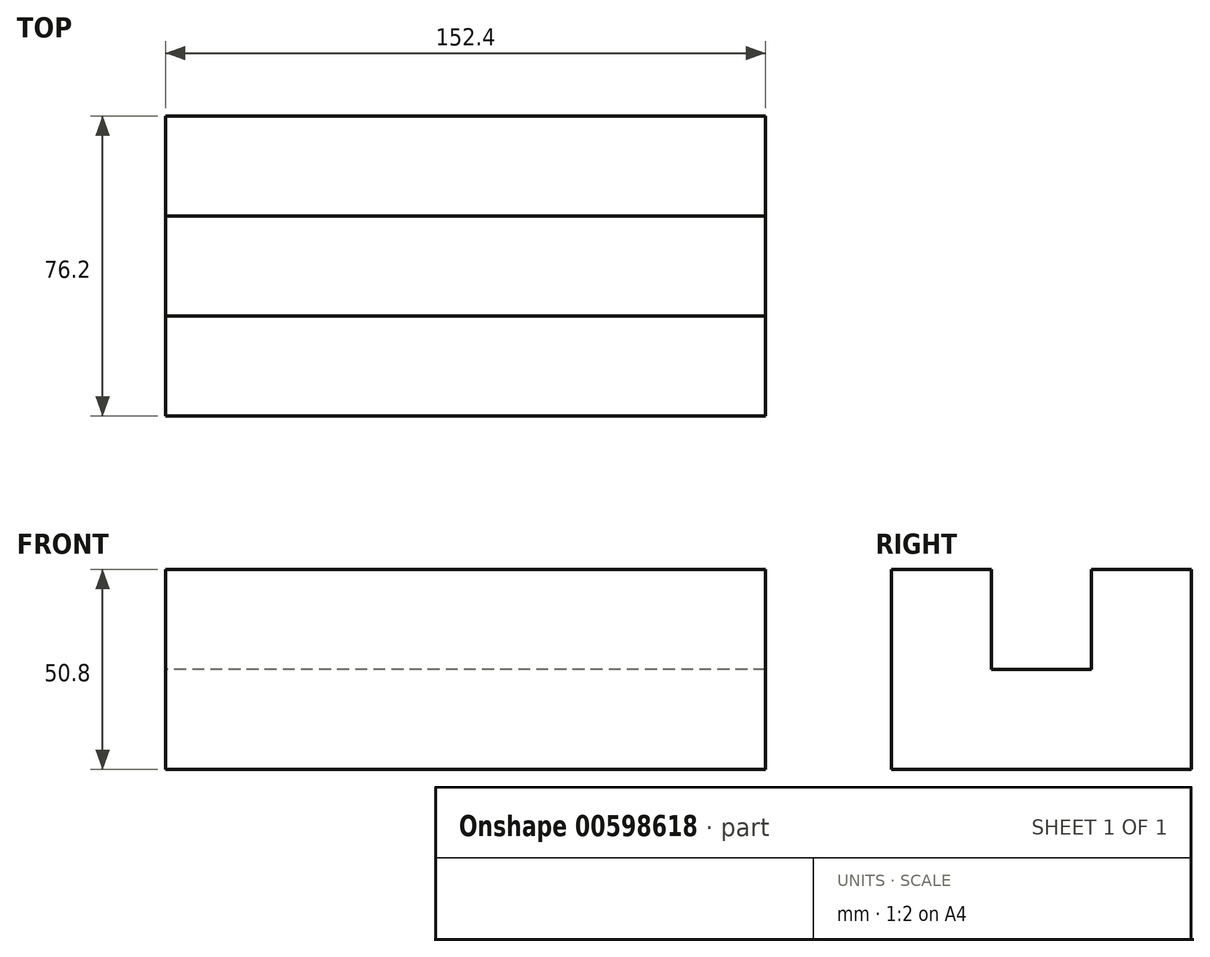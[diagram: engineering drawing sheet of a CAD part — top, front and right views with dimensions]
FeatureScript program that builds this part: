
annotation { "Feature Type Name" : "Feature", "Feature Type Description" : "" }
export const myFeature = defineFeature(function(context is Context, id is Id, definition is map)
    precondition{}
    {
        {
            var Q0;
            Q0=qCreatedBy(makeId("Right.planeOp"),FACE);
            var sketch = newSketch(context, id + "F0", { "sketchPlane" : qUnion([Q0])});
            skLineSegment(sketch, "E0", {"start": v(0, 0) * mm, "end": v(76.2, 0) * mm});
            skLineSegment(sketch, "E1", {"start": v(76.2, 0) * mm, "end": v(76.2, 50.8) * mm});
            skLineSegment(sketch, "E2", {"start": v(76.2, 50.8) * mm, "end": v(50.8, 50.8) * mm});
            skLineSegment(sketch, "E3", {"start": v(50.8, 50.8) * mm, "end": v(50.8, 25.4) * mm});
            skLineSegment(sketch, "E4", {"start": v(50.8, 25.4) * mm, "end": v(25.4, 25.4) * mm});
            skLineSegment(sketch, "E5", {"start": v(25.4, 25.4) * mm, "end": v(25.4, 50.8) * mm});
            skLineSegment(sketch, "E6", {"start": v(25.4, 50.8) * mm, "end": v(0, 50.8) * mm});
            skLineSegment(sketch, "E7", {"start": v(0, 50.8) * mm, "end": v(0, 0) * mm});
            skSolve(sketch);
        }
        {
            var Q0;
            Q0=makeQuery(id+"F0.imprint","IMPRINT",FACE,{"disambiguationData":[TD([[makeQuery(id+"F0.imprint","IMPRINT",EDGE,{"derivedFrom":sQuery(id+"F0.wireOp",EDGE,"E0")}),1.0]])]});
            extrude(context, id + "F1", {"entities" : qUnion([Q0]), "depth" : 152.4 * mm, "offsetDistance" : 25.4 * mm});
        }
    });
